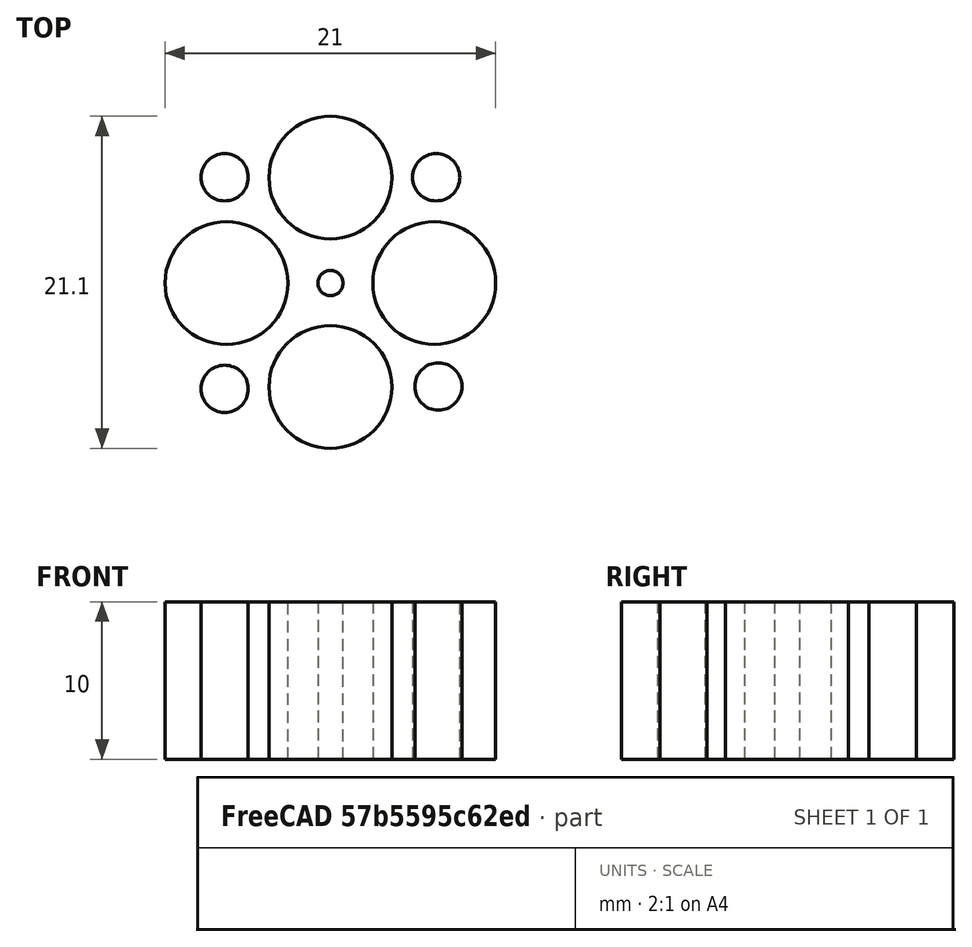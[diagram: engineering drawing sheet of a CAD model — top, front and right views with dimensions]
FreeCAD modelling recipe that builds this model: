
FCSTD DOCUMENT  (FreeCAD 0.19R0.19.2)
Label: 005
License: All rights reserved
LicenseURL: http://en.wikipedia.org/wiki/All_rights_reserved
objects: Sketcher::SketchObject×2, Part::Extrusion×1
note: 3 computed .brp shape members not serialized (recipe doc carries the construction recipe); baked Part::Feature solids carry a one-line shape summary decoded from their .brp

FEATURE [Sketcher::SketchObject] Sketch  label="holes"
  FullyConstrained = true
  sketch-geometry (9):
    g0: Circle CenterX=0 CenterY=0 CenterZ=0 NormalX=0 NormalY=0 NormalZ=1 AngleXU=0 Radius=0.8
    g1: Circle CenterX=0 CenterY=6.7 CenterZ=0 NormalX=0 NormalY=0 NormalZ=1 AngleXU=0 Radius=3.9
    g2: Circle CenterX=6.6 CenterY=0 CenterZ=0 NormalX=0 NormalY=0 NormalZ=1 AngleXU=0 Radius=3.9
    g3: Circle CenterX=-6.6 CenterY=0 CenterZ=0 NormalX=0 NormalY=0 NormalZ=1 AngleXU=0 Radius=3.9
    g4: Circle CenterX=0 CenterY=-6.6 CenterZ=0 NormalX=0 NormalY=0 NormalZ=1 AngleXU=0 Radius=3.9
    g5: Circle CenterX=6.71751 CenterY=6.71751 CenterZ=0 NormalX=0 NormalY=0 NormalZ=1 AngleXU=0 Radius=1.5
    g6: Circle CenterX=-6.71751 CenterY=-6.71751 CenterZ=0 NormalX=0 NormalY=0 NormalZ=1 AngleXU=0 Radius=1.5
    g7: Circle CenterX=-6.71751 CenterY=6.71751 CenterZ=0 NormalX=0 NormalY=0 NormalZ=1 AngleXU=0 Radius=1.5
    g8: Circle CenterX=6.86196 CenterY=-6.56989 CenterZ=0 NormalX=0 NormalY=0 NormalZ=1 AngleXU=0 Radius=1.5
  constraints (9):
    c: Block(g5)
    c: Block(g2)
    c: Block(g1)
    c: Block(g7)
    c: Block(g3)
    c: Block(g6)
    c: Block(g4)
    c: Block(g0)
    c: Block(g8)
FEATURE [Part::Extrusion] Extrude
  Base = -> Sketch
  Dir = (0,0,1)
  DirMode = 2
  FaceMakerClass = Part::FaceMakerBullseye
  LengthFwd = 10
  LengthRev = 0
  Solid = true
  Symmetric = false
FEATURE [Sketcher::SketchObject] Sketch001
  FullyConstrained = false
  Placement = pos=(0,0,0) rot=(0.57735,0.57735,0.57735;2.0944rad)
  sketch-geometry (28):
    g0: LineSegment StartX=0 StartY=0 StartZ=0 EndX=12.5 EndY=0 EndZ=0
    g1: LineSegment StartX=-1.6 StartY=4 StartZ=0 EndX=1.6 EndY=4 EndZ=0
    g2: LineSegment StartX=-1.6 StartY=-4 StartZ=0 EndX=1.6 EndY=-4 EndZ=0
    g3: Circle CenterX=-1.6 CenterY=4 CenterZ=0 NormalX=0 NormalY=0 NormalZ=1 AngleXU=0 Radius=1
    g4: Circle CenterX=-1.6 CenterY=2.5 CenterZ=0 NormalX=0 NormalY=0 NormalZ=1 AngleXU=0 Radius=1
    g5: Circle CenterX=-3.6 CenterY=2.5 CenterZ=0 NormalX=0 NormalY=0 NormalZ=1 AngleXU=0 Radius=1
    g6: BSplineCurve PolesCount=3 KnotsCount=2 Degree=2 IsPeriodic=0
    g7: GeomPoint X=-1.6 Y=4 Z=0
    g8: GeomPoint X=-3.6 Y=2.5 Z=0
    g9: Circle CenterX=-3.6 CenterY=-2.5 CenterZ=0 NormalX=0 NormalY=0 NormalZ=1 AngleXU=0 Radius=1
    g10: Circle CenterX=-1.6 CenterY=-2.5 CenterZ=0 NormalX=0 NormalY=0 NormalZ=1 AngleXU=0 Radius=1
    g11: Circle CenterX=-1.6 CenterY=-4 CenterZ=0 NormalX=0 NormalY=0 NormalZ=1 AngleXU=0 Radius=1
    g12: BSplineCurve PolesCount=3 KnotsCount=2 Degree=2 IsPeriodic=0
    g13: GeomPoint X=-3.6 Y=-2.5 Z=0
    g14: GeomPoint X=-1.6 Y=-4 Z=0
    g15: LineSegment StartX=0 StartY=0 StartZ=0 EndX=1.6 EndY=0 EndZ=0
    g16: Circle CenterX=1.6 CenterY=4 CenterZ=0 NormalX=0 NormalY=0 NormalZ=1 AngleXU=0 Radius=1
    g17: Circle CenterX=1.6 CenterY=2.5 CenterZ=0 NormalX=0 NormalY=0 NormalZ=1 AngleXU=0 Radius=1
    g18: Circle CenterX=3.6 CenterY=2.5 CenterZ=0 NormalX=0 NormalY=0 NormalZ=1 AngleXU=0 Radius=1
    g19: BSplineCurve PolesCount=3 KnotsCount=2 Degree=2 IsPeriodic=0
    g20: GeomPoint X=1.6 Y=4 Z=0
    g21: GeomPoint X=3.6 Y=2.5 Z=0
    g22: Circle CenterX=1.6 CenterY=-4 CenterZ=0 NormalX=0 NormalY=0 NormalZ=1 AngleXU=0 Radius=1
    g23: Circle CenterX=1.6 CenterY=-2.5 CenterZ=0 NormalX=0 NormalY=0 NormalZ=1 AngleXU=0 Radius=1
    g24: Circle CenterX=3.6 CenterY=-2.5 CenterZ=0 NormalX=0 NormalY=0 NormalZ=1 AngleXU=0 Radius=1
    g25: BSplineCurve PolesCount=3 KnotsCount=2 Degree=2 IsPeriodic=0
    g26: GeomPoint X=1.6 Y=-4 Z=0
    g27: GeomPoint X=3.6 Y=-2.5 Z=0
  constraints (50):
    c: Horizontal(g0)
    c: Distance(g0) = 12.5
    c: Coincident(g0,g-1)
    c: Horizontal(g1)
    c: Distance(g1) = 3.2
    c: Horizontal(g2)
    c: Equal(g1,g2) = 3.2
    c: Weight(g3) = 1
    c: Equal(g3,g4)
    c: Equal(g3,g5)
    c: InternalAlignment(g3,g6)
    c: InternalAlignment(g4,g6)
    c: InternalAlignment(g5,g6)
    c: InternalAlignment(g7,g6)
    c: InternalAlignment(g8,g6)
    c: Block(g2)
    c: Block(g1)
    c: Block(g6)
    c: Weight(g9) = 1
    c: Equal(g9,g10)
    c: Equal(g9,g11)
    c: Coincident(g12,g2)
    c: InternalAlignment(g9,g12)
    c: InternalAlignment(g10,g12)
    c: InternalAlignment(g11,g12)
    c: InternalAlignment(g13,g12)
    c: InternalAlignment(g14,g12)
    c: Horizontal(g15)
    c: Distance(g15) = 1.6
    c: Coincident(g15,g0)
    c: Coincident(g19,g1)
    c: Weight(g16) = 1
    c: Equal(g16,g17)
    c: Equal(g16,g18)
    c: InternalAlignment(g16,g19)
    c: InternalAlignment(g17,g19)
    c: InternalAlignment(g18,g19)
    c: InternalAlignment(g20,g19)
    c: InternalAlignment(g21,g19)
    c: Coincident(g25,g2)
    c: Weight(g22) = 1
    c: Equal(g22,g23)
    c: Equal(g22,g24)
    c: InternalAlignment(g22,g25)
    c: InternalAlignment(g23,g25)
    c: InternalAlignment(g24,g25)
    c: InternalAlignment(g26,g25)
    c: InternalAlignment(g27,g25)
    c: Block(g19)
    c: Block(g25)
